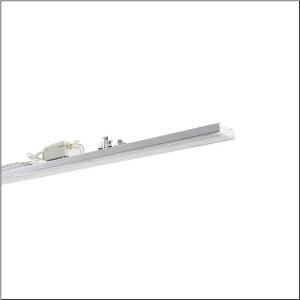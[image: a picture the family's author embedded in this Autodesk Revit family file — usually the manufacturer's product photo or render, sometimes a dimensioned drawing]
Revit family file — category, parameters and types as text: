
# Revit family: licross_11_recessed_ho_51te18mn4d5m
name_source: partatom
category: Lighting Fixtures
units: mm (PartAtom-declared; Revit-internal decimal feet)

## family parameters
Cut with Voids When Loaded = No
Host = Face
Light Source = No
Part Type = Normal
Room Calculation Point = No
Round Connector Dimension = Use Diameter
Shared = No

## types (1)
- --- (1 x LED, 13950 lm, 74.5 W, 4000K)
    Apparent Load = 75 VA
    CIE Flux Codes = 78 94 99 100 100
    Color Rendering = 80
    Color Temperature = 4000K
    Default Elevation = 1800 mm
    Description = Licross 11 Recessed HO, luminaire insert, of sheet steel, galvanised, coil coated, white, length: 1.500mm, width: 66mm, height: 67mm, LED rated luminous flux: 13.950lm, light colour: 840, SDCM (Standard Deviation of Colour Matching)MacAdam ≤ 2 SDCM (initial), control gear: ON/OFF Multilumen, with plug, 3-pole, with phase selection, mains connection: 220..240V, AC, 50/60Hz, rated input power: 75W, internal wiring halogen-free, primary light control with lens, of plastic, primary optical cover: cover, of PMMA, light emission: direct distribution, primary light characteristic: symmetric, protection rating (complete): IP54, insulation class (complete): insulation class I (protective earthing), certification: CE, ENEC, VDE, UKCA, protection symbol: D if used in an environment with non-conductive dust loads with corresponding accessories, impact resistance: IK06, permissible ambient temperature for indoor applications: -35..+35°C, corresponds to IFS (International Featured Standards) requirements for safety and quality in the food industry, reducing of maximum allowable ambient temperature of 5°C with ceiling mounting, The light source and the operating device comply with the requirements of the Ecodesign Regulation (EU) 2019/2020 and are replaceable in accordance with this regulation, packaging unit: 1 piece
    Height = 58 mm
    Lamp = 1 x LED
    Lamp Light Flux = 13950 lm
    Lamp Power = 74.5 W
    Lamp count = 1
    Length = 1500 mm
    Luminous efficacy = 187 lm/W
    Manufacturer = Siteco
    ModVariant = No
    Model = 51TE18MN4D5M
    Mounting Place = Ceiling
    Mounting Type = Pendant
    Number of Poles = 1
    OnlyDefault = Yes
    Power Factor = 1
    Product Name = Licross 11 Recessed HO
    Product group = luminaire insert | ceiling pendant
    ProductGroupID = 901
    Protection Class = Protection class I
    Protection Degree = IP 54
    RLX_Detail_Level = 1
    RLX_Emergency_Light_Flux = 0 lm
    RLX_Emergency_Type = 0
    RLX_Emergency_Type_DB = No
    RlxData = <blob elided: 22541 chars, md5=35a66a29>
    Socket = socket
    Standby Power = 0 W
    System Light Flux = 13950 lm
    System Power = 75 W
    Type Comments = factory setting: luminous flux: 100 % | (A | C | E) | 174 mA
    Type Image = l_1296930.jpg
    URL = http://relux.com
    VarID = @adj_091123
    Voltage = 0 V
    Weight = 0.00 kg
    Width = 66 mm

## geometry (parser evidence)
native form markers: Blend x4, Sweep x9
no freeform markers — native parametric forms only
